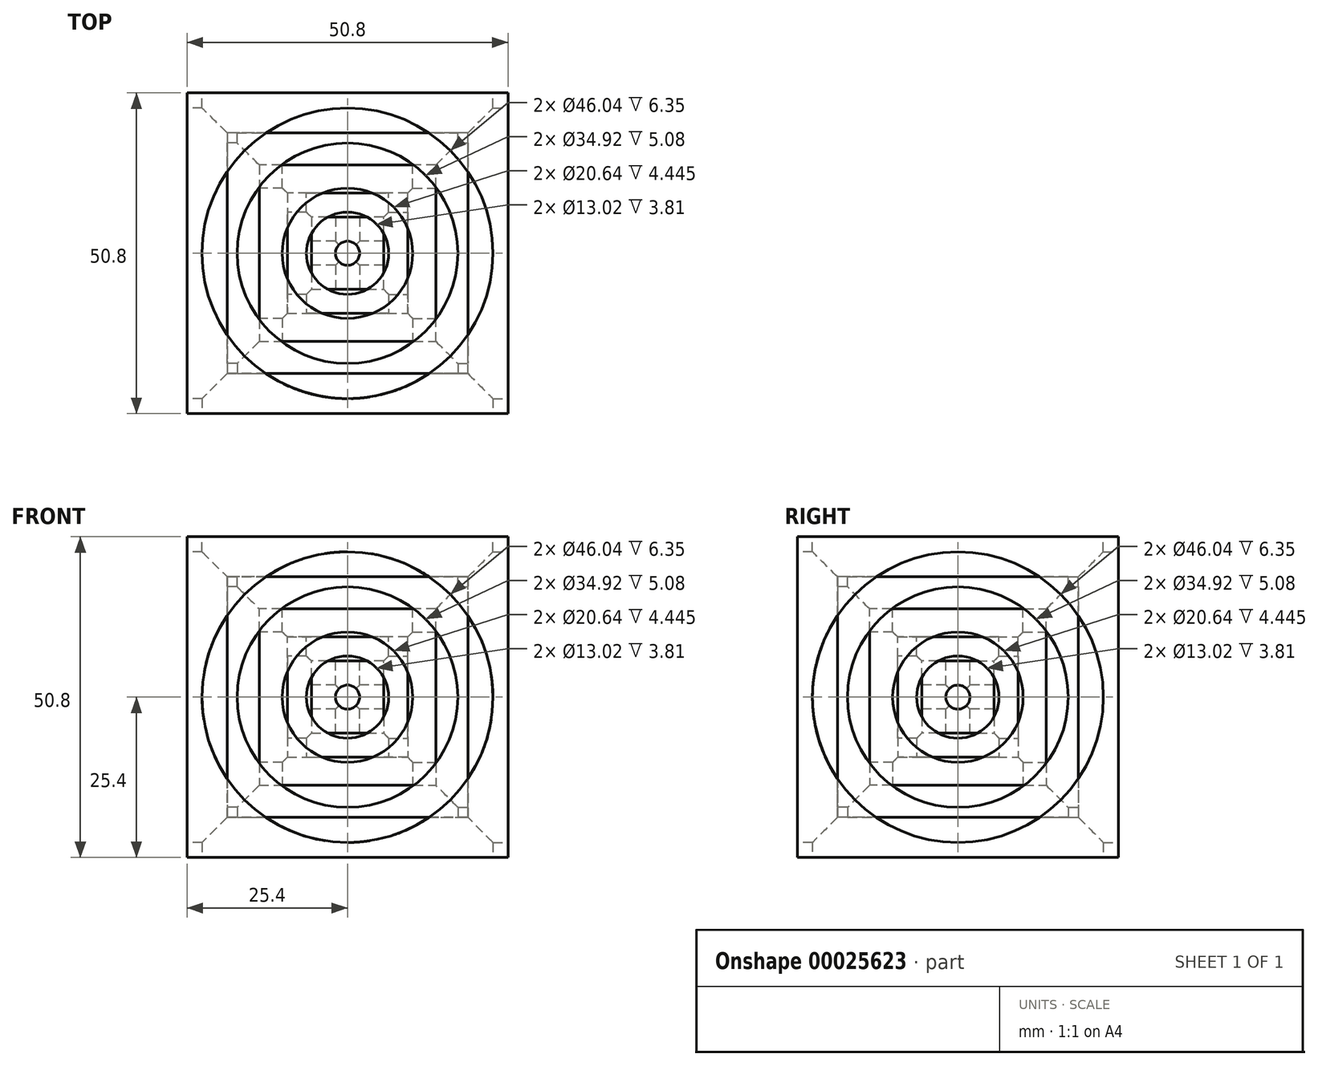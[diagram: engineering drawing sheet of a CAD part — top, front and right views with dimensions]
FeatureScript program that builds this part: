
annotation { "Feature Type Name" : "Feature", "Feature Type Description" : "" }
export const myFeature = defineFeature(function(context is Context, id is Id, definition is map)
    precondition{}
    {
        {
            var Q0;
            Q0=qCreatedBy(makeId("Front.planeOp"),FACE);
            var sketch = newSketch(context, id + "F0", { "sketchPlane" : qUnion([Q0])});
            skLineSegment(sketch, "E0.rect.bottom", {"start": v(25.4, 25.4) * mm, "end": v(-25.4, 25.4) * mm});
            skLineSegment(sketch, "E0.rect.top", {"start": v(25.4, -25.4) * mm, "end": v(-25.4, -25.4) * mm});
            skLineSegment(sketch, "E0.rect.left", {"start": v(25.4, 25.4) * mm, "end": v(25.4, -25.4) * mm});
            skLineSegment(sketch, "E0.rect.right", {"start": v(-25.4, 25.4) * mm, "end": v(-25.4, -25.4) * mm});
            skPoint(sketch, "E0.rect.middle", {"position": v(0, 0) * mm});
            skSolve(sketch);
        }
        {
            var Q0;
            Q0=makeQuery(id+"F0.imprint","IMPRINT",FACE,{"disambiguationData":[TD([[makeQuery(id+"F0.imprint","IMPRINT",EDGE,{"derivedFrom":sQuery(id+"F0.wireOp",EDGE,"E0.rect.bottom")}),1.0]])]});
            extrude(context, id + "F1", {"entities" : qUnion([Q0]), "depth" : 50.8 * mm});
        }
        {
            var Q0;
            Q0=makeQuery(id+"F1.opExtrude","CAP_FACE",FACE,{"disambiguationData":[OSD([sQuery(id+"F0.wireOp",EDGE,"E0.rect.bottom"),sQuery(id+"F0.wireOp",EDGE,"E0.rect.top"),sQuery(id+"F0.wireOp",EDGE,"E0.rect.left"),sQuery(id+"F0.wireOp",EDGE,"E0.rect.right")])],"isStart":false});
            var sketch = newSketch(context, id + "F2", { "sketchPlane" : qUnion([Q0])});
            skCircle(sketch, "E1", {"center": v(0, 0) * mm, "radius": 23.02 * mm});
            skSolve(sketch);
        }
        {
            var Q0;
            Q0 = qSketchRegion(id + "F2", true);
            extrude(context, id + "F3", {"entities" : qUnion([Q0]), "operationType" : NewBodyOperationType.REMOVE, "oppositeDirection" : true, "depth" : 6.35 * mm});
        }
        {
            var Q0;
            Q0=makeQuery(id+"F3.boolean.opBoolean","COPY",FACE,{"derivedFrom":makeQuery(id+"F3.opExtrude","CAP_FACE",FACE,{"disambiguationData":[OSD([sQuery(id+"F2.wireOp",EDGE,"E1")])],"isStart":false})});
            var sketch = newSketch(context, id + "F4", { "sketchPlane" : qUnion([Q0])});
            skCircle(sketch, "E2", {"center": v(0, 0) * mm, "radius": 17.46 * mm});
            skSolve(sketch);
        }
        {
            var Q0;
            Q0 = qSketchRegion(id + "F4", true);
            extrude(context, id + "F5", {"entities" : qUnion([Q0]), "operationType" : NewBodyOperationType.REMOVE, "oppositeDirection" : true, "depth" : 5.08 * mm});
        }
        {
            var Q0;
            Q0=makeQuery(id+"F5.boolean.opBoolean","COPY",FACE,{"derivedFrom":makeQuery(id+"F5.opExtrude","CAP_FACE",FACE,{"disambiguationData":[OSD([sQuery(id+"F4.wireOp",EDGE,"E2")])],"isStart":false})});
            var sketch = newSketch(context, id + "F6", { "sketchPlane" : qUnion([Q0])});
            skCircle(sketch, "E3", {"center": v(0, 0) * mm, "radius": 10.32 * mm});
            skSolve(sketch);
        }
        {
            var Q0;
            Q0=makeQuery(id+"F6.imprint","IMPRINT",FACE,{"disambiguationData":[TD([[makeQuery(id+"F6.imprint","IMPRINT",EDGE,{"derivedFrom":sQuery(id+"F6.wireOp",EDGE,"E3")}),1.0]])]});
            extrude(context, id + "F7", {"entities" : qUnion([Q0]), "operationType" : NewBodyOperationType.REMOVE, "oppositeDirection" : true, "depth" : 4.44 * mm});
        }
        {
            var Q0;
            Q0=makeQuery(id+"F7.boolean.opBoolean","COPY",FACE,{"derivedFrom":makeQuery(id+"F7.opExtrude","CAP_FACE",FACE,{"disambiguationData":[OSD([sQuery(id+"F6.wireOp",EDGE,"E3")])],"isStart":false})});
            var sketch = newSketch(context, id + "F8", { "sketchPlane" : qUnion([Q0])});
            skCircle(sketch, "E4", {"center": v(0, 0) * mm, "radius": 6.5 * mm});
            skSolve(sketch);
        }
        {
            var Q0;
            Q0=makeQuery(id+"F8.imprint","IMPRINT",FACE,{"disambiguationData":[TD([[makeQuery(id+"F8.imprint","IMPRINT",EDGE,{"derivedFrom":sQuery(id+"F8.wireOp",EDGE,"E4")}),1.0]])]});
            extrude(context, id + "F9", {"entities" : qUnion([Q0]), "operationType" : NewBodyOperationType.REMOVE, "oppositeDirection" : true, "depth" : 3.8 * mm});
        }
        {
            var Q0;
            Q0=makeQuery(id+"F9.boolean.opBoolean","COPY",FACE,{"derivedFrom":makeQuery(id+"F9.opExtrude","CAP_FACE",FACE,{"disambiguationData":[OSD([sQuery(id+"F8.wireOp",EDGE,"E4")])],"isStart":false})});
            var sketch = newSketch(context, id + "F10", { "sketchPlane" : qUnion([Q0])});
            skCircle(sketch, "E5", {"center": v(0, 0) * mm, "radius": 1.9 * mm});
            skSolve(sketch);
        }
        {
            var Q0;
            Q0=makeQuery(id+"F10.imprint","IMPRINT",FACE,{"disambiguationData":[TD([[makeQuery(id+"F10.imprint","IMPRINT",EDGE,{"derivedFrom":sQuery(id+"F10.wireOp",EDGE,"E5")}),1.0]])]});
            var Q1;
            Q1=sQuery(id+"F10.wireOp",EDGE,"E5");
            extrude(context, id + "F11", {"entities" : qUnion([Q0]), "operationType" : NewBodyOperationType.REMOVE, "surfaceEntities" : qUnion([Q1]), "endBound" : BoundingType.THROUGH_ALL, "oppositeDirection" : true, "depth" : 25.4 * mm});
        }
        {
            var Q0;
            Q0=makeQuery(id+"F1.opExtrude","CAP_FACE",FACE,{"disambiguationData":[OSD([sQuery(id+"F0.wireOp",EDGE,"E0.rect.bottom"),sQuery(id+"F0.wireOp",EDGE,"E0.rect.top"),sQuery(id+"F0.wireOp",EDGE,"E0.rect.left"),sQuery(id+"F0.wireOp",EDGE,"E0.rect.right")])],"isStart":true});
            var sketch = newSketch(context, id + "F12", { "sketchPlane" : qUnion([Q0]), "disableImprinting" : false});
            skCircle(sketch, "E6", {"center": v(0, 0) * mm, "radius": 23.02 * mm});
            skSolve(sketch);
        }
        {
            var Q0;
            Q0=makeQuery(id+"F12.imprint","IMPRINT",FACE,{"disambiguationData":[TD([[makeQuery(id+"F12.imprint","IMPRINT",EDGE,{"derivedFrom":sQuery(id+"F12.wireOp",EDGE,"E6")}),1.0]])]});
            extrude(context, id + "F13", {"entities" : qUnion([Q0]), "operationType" : NewBodyOperationType.REMOVE, "oppositeDirection" : true, "depth" : 6.35 * mm});
        }
        {
            var Q0;
            Q0=makeQuery(id+"F13.boolean.opBoolean","COPY",FACE,{"derivedFrom":makeQuery(id+"F13.opExtrude","CAP_FACE",FACE,{"disambiguationData":[OSD([sQuery(id+"F0.wireOp",EDGE,"E0.rect.bottom"),sQuery(id+"F0.wireOp",EDGE,"E0.rect.top"),sQuery(id+"F0.wireOp",EDGE,"E0.rect.left"),sQuery(id+"F0.wireOp",EDGE,"E0.rect.right"),sQuery(id+"F10.wireOp",EDGE,"E5"),sQuery(id+"F12.wireOp",EDGE,"E6")])],"isStart":false})});
            var sketch = newSketch(context, id + "F14", { "sketchPlane" : qUnion([Q0])});
            skCircle(sketch, "E7", {"center": v(0, 0) * mm, "radius": 17.46 * mm});
            skSolve(sketch);
        }
        {
            var Q0;
            Q0=makeQuery(id+"F14.imprint","IMPRINT",FACE,{"disambiguationData":[TD([[makeQuery(id+"F14.imprint","IMPRINT",EDGE,{"derivedFrom":sQuery(id+"F14.wireOp",EDGE,"E7")}),1.0]])]});
            extrude(context, id + "F15", {"entities" : qUnion([Q0]), "operationType" : NewBodyOperationType.REMOVE, "oppositeDirection" : true, "depth" : 5.08 * mm});
        }
        {
            var Q0;
            Q0=makeQuery(id+"F15.boolean.opBoolean","COPY",FACE,{"derivedFrom":makeQuery(id+"F15.opExtrude","CAP_FACE",FACE,{"disambiguationData":[OSD([sQuery(id+"F0.wireOp",EDGE,"E0.rect.bottom"),sQuery(id+"F0.wireOp",EDGE,"E0.rect.top"),sQuery(id+"F0.wireOp",EDGE,"E0.rect.left"),sQuery(id+"F0.wireOp",EDGE,"E0.rect.right"),sQuery(id+"F10.wireOp",EDGE,"E5"),sQuery(id+"F14.wireOp",EDGE,"E7")])],"isStart":false})});
            var sketch = newSketch(context, id + "F16", { "sketchPlane" : qUnion([Q0])});
            skCircle(sketch, "E8", {"center": v(0, 0) * mm, "radius": 10.32 * mm});
            skSolve(sketch);
        }
        {
            var Q0;
            Q0=makeQuery(id+"F16.imprint","IMPRINT",FACE,{"disambiguationData":[TD([[makeQuery(id+"F16.imprint","IMPRINT",EDGE,{"derivedFrom":sQuery(id+"F16.wireOp",EDGE,"E8")}),1.0]])]});
            extrude(context, id + "F17", {"entities" : qUnion([Q0]), "operationType" : NewBodyOperationType.REMOVE, "oppositeDirection" : true, "depth" : 4.44 * mm});
        }
        {
            var Q0;
            Q0=makeQuery(id+"F17.boolean.opBoolean","COPY",FACE,{"derivedFrom":makeQuery(id+"F17.opExtrude","CAP_FACE",FACE,{"disambiguationData":[OSD([sQuery(id+"F0.wireOp",EDGE,"E0.rect.bottom"),sQuery(id+"F0.wireOp",EDGE,"E0.rect.top"),sQuery(id+"F0.wireOp",EDGE,"E0.rect.left"),sQuery(id+"F0.wireOp",EDGE,"E0.rect.right"),sQuery(id+"F10.wireOp",EDGE,"E5"),sQuery(id+"F16.wireOp",EDGE,"E8")])],"isStart":false})});
            var sketch = newSketch(context, id + "F18", { "sketchPlane" : qUnion([Q0])});
            skCircle(sketch, "E9", {"center": v(0, 0) * mm, "radius": 6.5 * mm});
            skSolve(sketch);
        }
        {
            var Q0;
            Q0=makeQuery(id+"F18.imprint","IMPRINT",FACE,{"disambiguationData":[TD([[makeQuery(id+"F18.imprint","IMPRINT",EDGE,{"derivedFrom":sQuery(id+"F18.wireOp",EDGE,"E9")}),1.0]])]});
            extrude(context, id + "F19", {"entities" : qUnion([Q0]), "operationType" : NewBodyOperationType.REMOVE, "oppositeDirection" : true, "depth" : 3.8 * mm});
        }
        {
            var Q0;
            Q0=makeQuery(id+"F1.opExtrude","SWEPT_FACE",FACE,{"disambiguationData":[OSD([sQuery(id+"F0.wireOp",EDGE,"E0.rect.right")])]});
            var sketch = newSketch(context, id + "F20", { "sketchPlane" : qUnion([Q0]), "disableImprinting" : false});
            skCircle(sketch, "E10", {"center": v(25.4, 0) * mm, "radius": 23.02 * mm});
            skSolve(sketch);
        }
        {
            var Q0;
            Q0=makeQuery(id+"F20.imprint","IMPRINT",FACE,{"disambiguationData":[TD([[makeQuery(id+"F20.imprint","IMPRINT",EDGE,{"derivedFrom":sQuery(id+"F20.wireOp",EDGE,"E10")}),1.0]])]});
            extrude(context, id + "F21", {"entities" : qUnion([Q0]), "operationType" : NewBodyOperationType.REMOVE, "oppositeDirection" : true, "depth" : 6.35 * mm});
        }
        {
            var Q0;
            Q0=makeQuery(id+"F21.boolean.opBoolean","COPY",FACE,{"derivedFrom":makeQuery(id+"F21.opExtrude","CAP_FACE",FACE,{"disambiguationData":[OSD([sQuery(id+"F20.wireOp",EDGE,"E10")])],"isStart":false})});
            var sketch = newSketch(context, id + "F22", { "sketchPlane" : qUnion([Q0])});
            skCircle(sketch, "E11", {"center": v(25.4, 0) * mm, "radius": 17.46 * mm});
            skSolve(sketch);
        }
        {
            var Q0;
            Q0=makeQuery(id+"F22.imprint","IMPRINT",FACE,{"disambiguationData":[TD([[makeQuery(id+"F22.imprint","IMPRINT",EDGE,{"derivedFrom":sQuery(id+"F22.wireOp",EDGE,"E11")}),1.0]])]});
            extrude(context, id + "F23", {"entities" : qUnion([Q0]), "operationType" : NewBodyOperationType.REMOVE, "oppositeDirection" : true, "depth" : 5.08 * mm});
        }
        {
            var Q0;
            Q0=makeQuery(id+"F23.boolean.opBoolean","COPY",FACE,{"derivedFrom":makeQuery(id+"F23.opExtrude","CAP_FACE",FACE,{"disambiguationData":[OSD([sQuery(id+"F22.wireOp",EDGE,"E11")])],"isStart":false})});
            var sketch = newSketch(context, id + "F24", { "sketchPlane" : qUnion([Q0])});
            skCircle(sketch, "E12", {"center": v(25.4, 0) * mm, "radius": 10.32 * mm});
            skSolve(sketch);
        }
        {
            var Q0;
            Q0=makeQuery(id+"F24.imprint","IMPRINT",FACE,{"disambiguationData":[TD([[makeQuery(id+"F24.imprint","IMPRINT",EDGE,{"derivedFrom":sQuery(id+"F24.wireOp",EDGE,"E12")}),1.0]])]});
            extrude(context, id + "F25", {"entities" : qUnion([Q0]), "operationType" : NewBodyOperationType.REMOVE, "oppositeDirection" : true, "depth" : 4.44 * mm});
        }
        {
            var Q0;
            Q0=makeQuery(id+"F25.boolean.opBoolean","COPY",FACE,{"derivedFrom":makeQuery(id+"F25.opExtrude","CAP_FACE",FACE,{"disambiguationData":[OSD([sQuery(id+"F24.wireOp",EDGE,"E12")])],"isStart":false})});
            var sketch = newSketch(context, id + "F26", { "sketchPlane" : qUnion([Q0])});
            skCircle(sketch, "E13", {"center": v(25.4, 0) * mm, "radius": 6.5 * mm});
            skSolve(sketch);
        }
        {
            var Q0;
            Q0=makeQuery(id+"F26.imprint","IMPRINT",FACE,{"disambiguationData":[TD([[makeQuery(id+"F26.imprint","IMPRINT",EDGE,{"derivedFrom":sQuery(id+"F26.wireOp",EDGE,"E13")}),1.0]])]});
            extrude(context, id + "F27", {"entities" : qUnion([Q0]), "operationType" : NewBodyOperationType.REMOVE, "oppositeDirection" : true, "depth" : 3.8 * mm});
        }
        {
            var Q0;
            Q0=makeQuery(id+"F27.boolean.opBoolean","COPY",FACE,{"derivedFrom":makeQuery(id+"F27.opExtrude","CAP_FACE",FACE,{"disambiguationData":[OSD([sQuery(id+"F26.wireOp",EDGE,"E13")])],"isStart":false})});
            var sketch = newSketch(context, id + "F28", { "sketchPlane" : qUnion([Q0])});
            skCircle(sketch, "E14", {"center": v(25.4, 0) * mm, "radius": 1.9 * mm});
            skSolve(sketch);
        }
        {
            var Q0;
            Q0=makeQuery(id+"F28.imprint","IMPRINT",FACE,{"disambiguationData":[TD([[makeQuery(id+"F28.imprint","IMPRINT",EDGE,{"derivedFrom":sQuery(id+"F28.wireOp",EDGE,"E14")}),1.0]])]});
            extrude(context, id + "F29", {"entities" : qUnion([Q0]), "operationType" : NewBodyOperationType.REMOVE, "endBound" : BoundingType.THROUGH_ALL, "oppositeDirection" : true, "depth" : 127 * mm});
        }
        {
            var Q0;
            Q0=makeQuery(id+"F1.opExtrude","SWEPT_FACE",FACE,{"disambiguationData":[OSD([sQuery(id+"F0.wireOp",EDGE,"E0.rect.left")])]});
            var sketch = newSketch(context, id + "F30", { "sketchPlane" : qUnion([Q0]), "disableImprinting" : false});
            skCircle(sketch, "E15", {"center": v(-25.4, 0) * mm, "radius": 23.02 * mm});
            skSolve(sketch);
        }
        {
            var Q0;
            Q0=makeQuery(id+"F30.imprint","IMPRINT",FACE,{"disambiguationData":[TD([[makeQuery(id+"F30.imprint","IMPRINT",EDGE,{"derivedFrom":sQuery(id+"F30.wireOp",EDGE,"E15")}),1.0]])]});
            extrude(context, id + "F31", {"entities" : qUnion([Q0]), "operationType" : NewBodyOperationType.REMOVE, "oppositeDirection" : true, "depth" : 6.35 * mm});
        }
        {
            var Q0;
            Q0=makeQuery(id+"F31.boolean.opBoolean","COPY",FACE,{"derivedFrom":makeQuery(id+"F31.opExtrude","CAP_FACE",FACE,{"disambiguationData":[OSD([sQuery(id+"F0.wireOp",EDGE,"E0.rect.left"),sQuery(id+"F28.wireOp",EDGE,"E14"),sQuery(id+"F30.wireOp",EDGE,"E15")])],"isStart":false})});
            var sketch = newSketch(context, id + "F32", { "sketchPlane" : qUnion([Q0])});
            skCircle(sketch, "E16", {"center": v(-25.4, 0) * mm, "radius": 17.46 * mm});
            skSolve(sketch);
        }
        {
            var Q0;
            Q0=makeQuery(id+"F32.imprint","IMPRINT",FACE,{"disambiguationData":[TD([[makeQuery(id+"F32.imprint","IMPRINT",EDGE,{"derivedFrom":sQuery(id+"F32.wireOp",EDGE,"E16")}),1.0]])]});
            extrude(context, id + "F33", {"entities" : qUnion([Q0]), "operationType" : NewBodyOperationType.REMOVE, "oppositeDirection" : true, "depth" : 5.08 * mm});
        }
        {
            var Q0;
            Q0=makeQuery(id+"F33.boolean.opBoolean","COPY",FACE,{"derivedFrom":makeQuery(id+"F33.opExtrude","CAP_FACE",FACE,{"disambiguationData":[OSD([sQuery(id+"F0.wireOp",EDGE,"E0.rect.left"),sQuery(id+"F28.wireOp",EDGE,"E14"),sQuery(id+"F32.wireOp",EDGE,"E16")])],"isStart":false})});
            var sketch = newSketch(context, id + "F34", { "sketchPlane" : qUnion([Q0])});
            skCircle(sketch, "E17", {"center": v(-25.4, 0) * mm, "radius": 10.32 * mm});
            skSolve(sketch);
        }
        {
            var Q0;
            Q0=makeQuery(id+"F34.imprint","IMPRINT",FACE,{"disambiguationData":[TD([[makeQuery(id+"F34.imprint","IMPRINT",EDGE,{"derivedFrom":sQuery(id+"F34.wireOp",EDGE,"E17")}),1.0]])]});
            extrude(context, id + "F35", {"entities" : qUnion([Q0]), "operationType" : NewBodyOperationType.REMOVE, "oppositeDirection" : true, "depth" : 4.44 * mm});
        }
        {
            var Q0;
            Q0=makeQuery(id+"F35.boolean.opBoolean","COPY",FACE,{"derivedFrom":makeQuery(id+"F35.opExtrude","CAP_FACE",FACE,{"disambiguationData":[OSD([sQuery(id+"F0.wireOp",EDGE,"E0.rect.left"),sQuery(id+"F28.wireOp",EDGE,"E14"),sQuery(id+"F34.wireOp",EDGE,"E17")])],"isStart":false})});
            var sketch = newSketch(context, id + "F36", { "sketchPlane" : qUnion([Q0])});
            skCircle(sketch, "E18", {"center": v(-25.4, 0) * mm, "radius": 6.5 * mm});
            skSolve(sketch);
        }
        {
            var Q0;
            Q0=makeQuery(id+"F36.imprint","IMPRINT",FACE,{"disambiguationData":[TD([[makeQuery(id+"F36.imprint","IMPRINT",EDGE,{"derivedFrom":sQuery(id+"F36.wireOp",EDGE,"E18")}),1.0]])]});
            extrude(context, id + "F37", {"entities" : qUnion([Q0]), "operationType" : NewBodyOperationType.REMOVE, "oppositeDirection" : true, "depth" : 3.8 * mm});
        }
        {
            var Q0;
            Q0=makeQuery(id+"F1.opExtrude","SWEPT_FACE",FACE,{"disambiguationData":[OSD([sQuery(id+"F0.wireOp",EDGE,"E0.rect.bottom")])]});
            var sketch = newSketch(context, id + "F38", { "sketchPlane" : qUnion([Q0]), "disableImprinting" : false});
            skCircle(sketch, "E19", {"center": v(0, -25.4) * mm, "radius": 23.02 * mm});
            skSolve(sketch);
        }
        {
            var Q0;
            Q0=makeQuery(id+"F38.imprint","IMPRINT",FACE,{"disambiguationData":[TD([[makeQuery(id+"F38.imprint","IMPRINT",EDGE,{"derivedFrom":sQuery(id+"F38.wireOp",EDGE,"E19")}),1.0]])]});
            extrude(context, id + "F39", {"entities" : qUnion([Q0]), "operationType" : NewBodyOperationType.REMOVE, "oppositeDirection" : true, "depth" : 6.35 * mm});
        }
        {
            var Q0;
            Q0=makeQuery(id+"F39.boolean.opBoolean","COPY",FACE,{"derivedFrom":makeQuery(id+"F39.opExtrude","CAP_FACE",FACE,{"disambiguationData":[OSD([sQuery(id+"F38.wireOp",EDGE,"E19")])],"isStart":false})});
            var sketch = newSketch(context, id + "F40", { "sketchPlane" : qUnion([Q0])});
            skCircle(sketch, "E20", {"center": v(0, -25.4) * mm, "radius": 17.46 * mm});
            skSolve(sketch);
        }
        {
            var Q0;
            Q0=makeQuery(id+"F40.imprint","IMPRINT",FACE,{"disambiguationData":[TD([[makeQuery(id+"F40.imprint","IMPRINT",EDGE,{"derivedFrom":sQuery(id+"F40.wireOp",EDGE,"E20")}),1.0]])]});
            extrude(context, id + "F41", {"entities" : qUnion([Q0]), "operationType" : NewBodyOperationType.REMOVE, "oppositeDirection" : true, "depth" : 5.08 * mm});
        }
        {
            var Q0;
            Q0=makeQuery(id+"F41.boolean.opBoolean","COPY",FACE,{"derivedFrom":makeQuery(id+"F41.opExtrude","CAP_FACE",FACE,{"disambiguationData":[OSD([sQuery(id+"F40.wireOp",EDGE,"E20")])],"isStart":false})});
            var sketch = newSketch(context, id + "F42", { "sketchPlane" : qUnion([Q0])});
            skCircle(sketch, "E21", {"center": v(0, -25.4) * mm, "radius": 10.32 * mm});
            skSolve(sketch);
        }
        {
            var Q0;
            Q0=makeQuery(id+"F42.imprint","IMPRINT",FACE,{"disambiguationData":[TD([[makeQuery(id+"F42.imprint","IMPRINT",EDGE,{"derivedFrom":sQuery(id+"F42.wireOp",EDGE,"E21")}),1.0]])]});
            extrude(context, id + "F43", {"entities" : qUnion([Q0]), "operationType" : NewBodyOperationType.REMOVE, "oppositeDirection" : true, "depth" : 4.44 * mm});
        }
        {
            var Q0;
            Q0=makeQuery(id+"F43.boolean.opBoolean","COPY",FACE,{"derivedFrom":makeQuery(id+"F43.opExtrude","CAP_FACE",FACE,{"disambiguationData":[OSD([sQuery(id+"F42.wireOp",EDGE,"E21")])],"isStart":false})});
            var sketch = newSketch(context, id + "F44", { "sketchPlane" : qUnion([Q0])});
            skCircle(sketch, "E22", {"center": v(0, -25.4) * mm, "radius": 6.5 * mm});
            skSolve(sketch);
        }
        {
            var Q0;
            Q0=makeQuery(id+"F44.imprint","IMPRINT",FACE,{"disambiguationData":[TD([[makeQuery(id+"F44.imprint","IMPRINT",EDGE,{"derivedFrom":sQuery(id+"F44.wireOp",EDGE,"E22")}),1.0]])]});
            extrude(context, id + "F45", {"entities" : qUnion([Q0]), "operationType" : NewBodyOperationType.REMOVE, "oppositeDirection" : true, "depth" : 3.8 * mm});
        }
        {
            var Q0;
            Q0=makeQuery(id+"F45.boolean.opBoolean","COPY",FACE,{"derivedFrom":makeQuery(id+"F45.opExtrude","CAP_FACE",FACE,{"disambiguationData":[OSD([sQuery(id+"F44.wireOp",EDGE,"E22")])],"isStart":false})});
            var sketch = newSketch(context, id + "F46", { "sketchPlane" : qUnion([Q0])});
            skCircle(sketch, "E23", {"center": v(0, -25.4) * mm, "radius": 1.9 * mm});
            skSolve(sketch);
        }
        {
            var Q0;
            Q0=makeQuery(id+"F46.imprint","IMPRINT",FACE,{"disambiguationData":[TD([[makeQuery(id+"F46.imprint","IMPRINT",EDGE,{"derivedFrom":sQuery(id+"F46.wireOp",EDGE,"E23")}),1.0]])]});
            extrude(context, id + "F47", {"entities" : qUnion([Q0]), "operationType" : NewBodyOperationType.REMOVE, "endBound" : BoundingType.THROUGH_ALL, "oppositeDirection" : true, "depth" : 25.4 * mm});
        }
        {
            var Q0;
            Q0=makeQuery(id+"F1.opExtrude","SWEPT_FACE",FACE,{"disambiguationData":[OSD([sQuery(id+"F0.wireOp",EDGE,"E0.rect.top")])]});
            var sketch = newSketch(context, id + "F48", { "sketchPlane" : qUnion([Q0]), "disableImprinting" : false});
            skCircle(sketch, "E24", {"center": v(0, 25.4) * mm, "radius": 23.02 * mm});
            skSolve(sketch);
        }
        {
            var Q0;
            Q0=makeQuery(id+"F48.imprint","IMPRINT",FACE,{"disambiguationData":[TD([[makeQuery(id+"F48.imprint","IMPRINT",EDGE,{"derivedFrom":sQuery(id+"F48.wireOp",EDGE,"E24")}),1.0]])]});
            extrude(context, id + "F49", {"entities" : qUnion([Q0]), "operationType" : NewBodyOperationType.REMOVE, "oppositeDirection" : true, "depth" : 6.35 * mm});
        }
        {
            var Q0;
            Q0=makeQuery(id+"F49.boolean.opBoolean","COPY",FACE,{"derivedFrom":makeQuery(id+"F49.opExtrude","CAP_FACE",FACE,{"disambiguationData":[OSD([sQuery(id+"F0.wireOp",EDGE,"E0.rect.top"),sQuery(id+"F46.wireOp",EDGE,"E23"),sQuery(id+"F48.wireOp",EDGE,"E24")])],"isStart":false})});
            var sketch = newSketch(context, id + "F50", { "sketchPlane" : qUnion([Q0])});
            skCircle(sketch, "E25", {"center": v(0, 25.4) * mm, "radius": 17.46 * mm});
            skSolve(sketch);
        }
        {
            var Q0;
            Q0=makeQuery(id+"F50.imprint","IMPRINT",FACE,{"disambiguationData":[TD([[makeQuery(id+"F50.imprint","IMPRINT",EDGE,{"derivedFrom":sQuery(id+"F50.wireOp",EDGE,"E25")}),1.0]])]});
            extrude(context, id + "F51", {"entities" : qUnion([Q0]), "operationType" : NewBodyOperationType.REMOVE, "oppositeDirection" : true, "depth" : 5.08 * mm});
        }
        {
            var Q0;
            Q0=makeQuery(id+"F51.boolean.opBoolean","COPY",FACE,{"derivedFrom":makeQuery(id+"F51.opExtrude","CAP_FACE",FACE,{"disambiguationData":[OSD([sQuery(id+"F0.wireOp",EDGE,"E0.rect.top"),sQuery(id+"F46.wireOp",EDGE,"E23"),sQuery(id+"F50.wireOp",EDGE,"E25")])],"isStart":false})});
            var sketch = newSketch(context, id + "F52", { "sketchPlane" : qUnion([Q0])});
            skCircle(sketch, "E26", {"center": v(0, 25.4) * mm, "radius": 10.32 * mm});
            skSolve(sketch);
        }
        {
            var Q0;
            Q0=makeQuery(id+"F52.imprint","IMPRINT",FACE,{"disambiguationData":[TD([[makeQuery(id+"F52.imprint","IMPRINT",EDGE,{"derivedFrom":sQuery(id+"F52.wireOp",EDGE,"E26")}),1.0]])]});
            extrude(context, id + "F53", {"entities" : qUnion([Q0]), "operationType" : NewBodyOperationType.REMOVE, "oppositeDirection" : true, "depth" : 4.44 * mm});
        }
        {
            var Q0;
            Q0=makeQuery(id+"F53.boolean.opBoolean","COPY",FACE,{"derivedFrom":makeQuery(id+"F53.opExtrude","CAP_FACE",FACE,{"disambiguationData":[OSD([sQuery(id+"F0.wireOp",EDGE,"E0.rect.top"),sQuery(id+"F46.wireOp",EDGE,"E23"),sQuery(id+"F52.wireOp",EDGE,"E26")])],"isStart":false})});
            var sketch = newSketch(context, id + "F54", { "sketchPlane" : qUnion([Q0])});
            skCircle(sketch, "E27", {"center": v(0, 25.4) * mm, "radius": 6.5 * mm});
            skSolve(sketch);
        }
        {
            var Q0;
            Q0=makeQuery(id+"F54.imprint","IMPRINT",FACE,{"disambiguationData":[TD([[makeQuery(id+"F54.imprint","IMPRINT",EDGE,{"derivedFrom":sQuery(id+"F54.wireOp",EDGE,"E27")}),1.0]])]});
            extrude(context, id + "F55", {"entities" : qUnion([Q0]), "operationType" : NewBodyOperationType.REMOVE, "oppositeDirection" : true, "depth" : 3.8 * mm});
        }
    });
